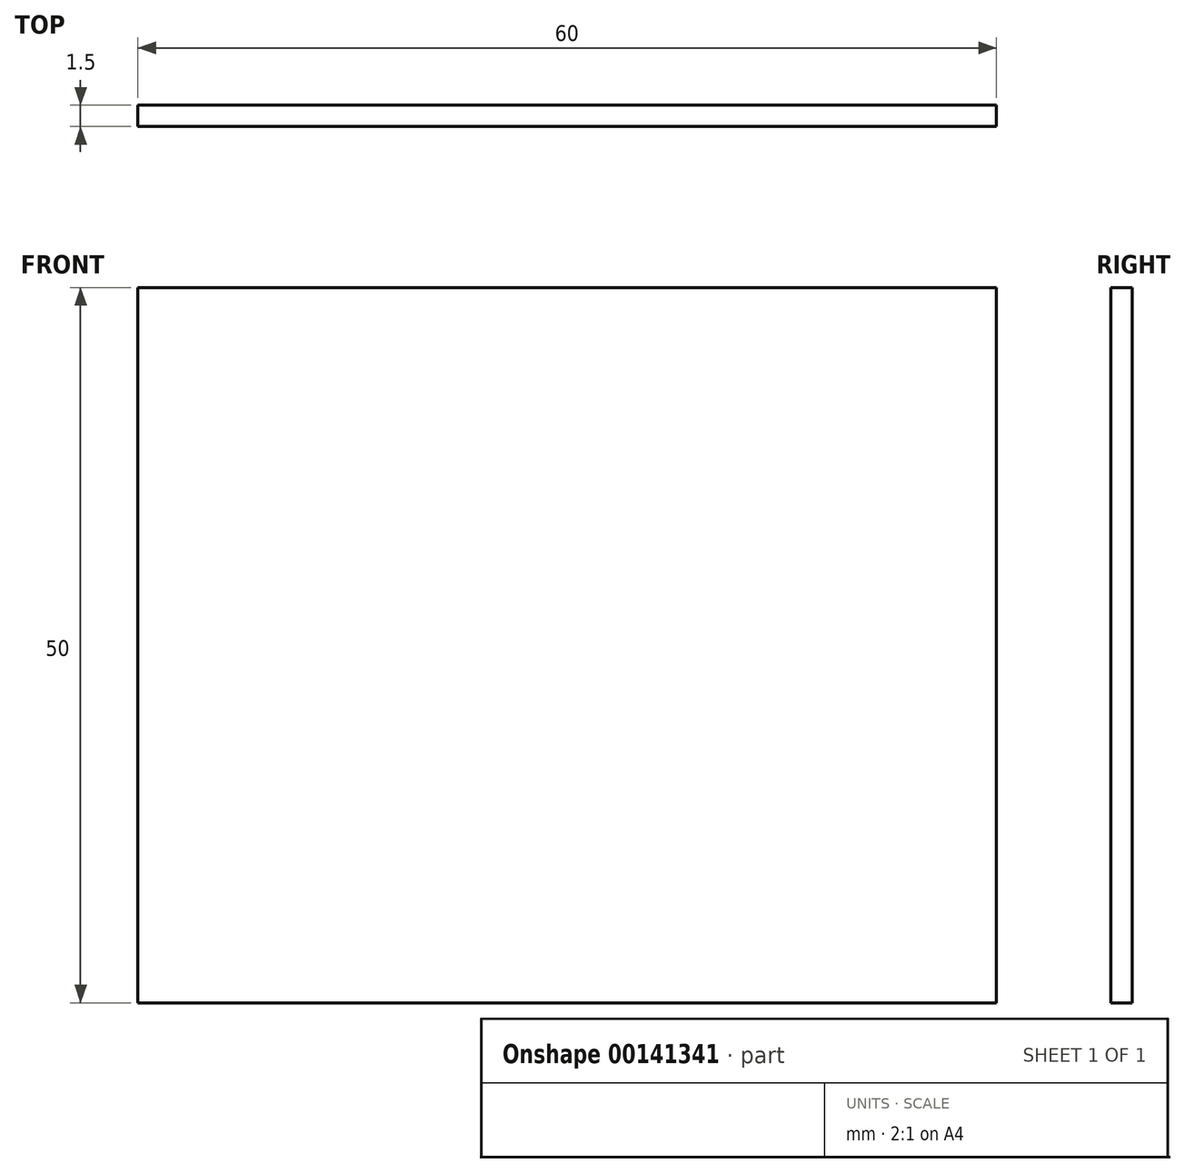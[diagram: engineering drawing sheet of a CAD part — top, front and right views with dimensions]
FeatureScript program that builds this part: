
annotation { "Feature Type Name" : "Feature", "Feature Type Description" : "" }
export const myFeature = defineFeature(function(context is Context, id is Id, definition is map)
    precondition{}
    {
        {
            var Q0;
            Q0=qCreatedBy(makeId("Front.planeOp"),FACE);
            var sketch = newSketch(context, id + "F0", { "sketchPlane" : qUnion([Q0])});
            skLineSegment(sketch, "E0.bottom", {"start": v(30, -25) * mm, "end": v(-30, -25) * mm});
            skLineSegment(sketch, "E0.top", {"start": v(30, 25) * mm, "end": v(-30, 25) * mm});
            skLineSegment(sketch, "E0.left", {"start": v(30, -25) * mm, "end": v(30, 25) * mm});
            skLineSegment(sketch, "E0.right", {"start": v(-30, -25) * mm, "end": v(-30, 25) * mm});
            skPoint(sketch, "E0.middle", {"position": v(0, 0) * mm});
            skSolve(sketch);
        }
        {
            var Q0;
            Q0 = qSketchRegion(id + "F0", true);
            extrude(context, id + "F1", {"entities" : qUnion([Q0]), "depth" : 1.5 * mm});
        }
    });
